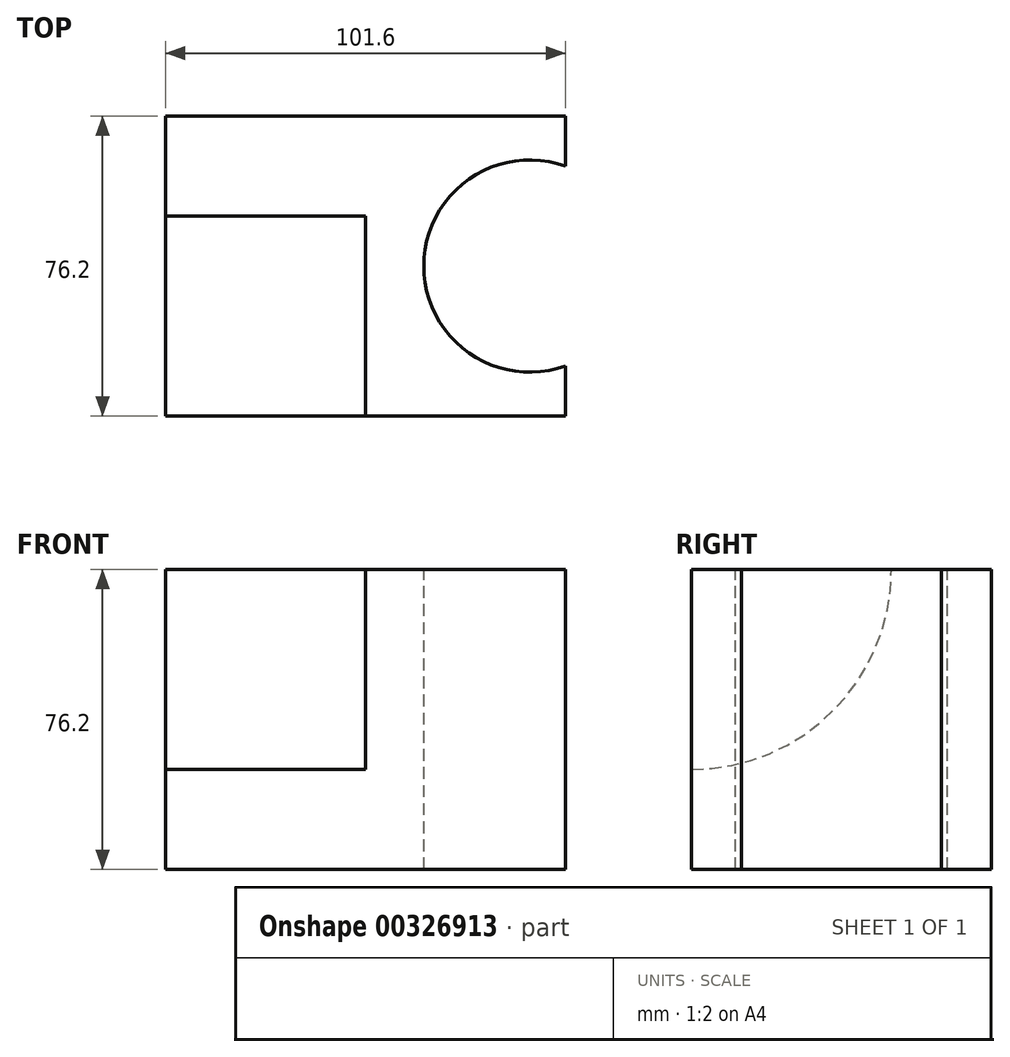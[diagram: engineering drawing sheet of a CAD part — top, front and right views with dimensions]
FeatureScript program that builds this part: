
annotation { "Feature Type Name" : "Feature", "Feature Type Description" : "" }
export const myFeature = defineFeature(function(context is Context, id is Id, definition is map)
    precondition{}
    {
        {
            var Q0;
            Q0=qCreatedBy(makeId("Front.planeOp"),FACE);
            var sketch = newSketch(context, id + "F0", { "sketchPlane" : qUnion([Q0])});
            skLineSegment(sketch, "E0", {"start": v(-48.15, -47.94) * mm, "end": v(53.45, -47.94) * mm});
            skLineSegment(sketch, "E1", {"start": v(-48.15, -47.94) * mm, "end": v(-48.15, -35.24) * mm});
            skLineSegment(sketch, "E2", {"start": v(-48.15, -35.24) * mm, "end": v(53.45, -35.24) * mm});
            skLineSegment(sketch, "E3", {"start": v(53.45, -35.24) * mm, "end": v(53.45, -47.94) * mm});
            skSolve(sketch);
        }
        {
            var Q0;
            Q0=makeQuery(id+"F0.imprint","IMPRINT",FACE,{"disambiguationData":[TD([[makeQuery(id+"F0.imprint","IMPRINT",EDGE,{"derivedFrom":sQuery(id+"F0.wireOp",EDGE,"E0")}),1.0]])]});
            extrude(context, id + "F1", {"entities" : qUnion([Q0]), "depth" : 76.2 * mm});
        }
        {
            var Q0;
            Q0=makeQuery(id+"F1.opExtrude","SWEPT_FACE",FACE,{"disambiguationData":[OSD([sQuery(id+"F0.wireOp",EDGE,"E2")])]});
            extrude(context, id + "F2", {"entities" : qUnion([Q0]), "operationType" : NewBodyOperationType.ADD, "depth" : 63.5 * mm});
        }
        {
            var Q0;
            Q0=makeQuery(id+"F2.opExtrude","CAP_FACE",FACE,{"disambiguationData":[OSD([sQuery(id+"F0.wireOp",EDGE,"E2")])],"isStart":false});
            var sketch = newSketch(context, id + "F3", { "sketchPlane" : qUnion([Q0])});
            skLineSegment(sketch, "E4", {"start": v(53.45, 0) * mm, "end": v(53.45, -12.7) * mm});
            skLineSegment(sketch, "E5", {"start": v(53.45, -76.2) * mm, "end": v(53.45, -63.5) * mm});
            skArc(sketch, "E6", {"start": v(53.45, -12.7) * mm, "mid": v(17.45, -38.1) * mm, "end": v(53.45, -63.5) * mm});
            skSolve(sketch);
        }
        {
            var Q0;
            {var subQ0=sQuery(id+"F3.wireOp",EDGE,"E6");Q0=makeQuery(id+"F3.imprint","IMPRINT",FACE,{"disambiguationData":[TD([[makeQuery(id+"F3.imprint","IMPRINT",EDGE,{"derivedFrom":subQ0}),1.0]])]});}
            extrude(context, id + "F4", {"entities" : qUnion([Q0]), "operationType" : NewBodyOperationType.REMOVE, "oppositeDirection" : true, "depth" : 127 * mm});
        }
        {
            var Q0;
            Q0=makeQuery(id+"F2.opExtrude","CAP_FACE",FACE,{"disambiguationData":[OSD([sQuery(id+"F0.wireOp",EDGE,"E2")])],"isStart":false});
            var sketch = newSketch(context, id + "F5", { "sketchPlane" : qUnion([Q0])});
            skLineSegment(sketch, "E7", {"start": v(-48.15, 0) * mm, "end": v(-48.15, -25.4) * mm});
            skLineSegment(sketch, "E8", {"start": v(-48.15, -25.4) * mm, "end": v(2.65, -25.4) * mm});
            skLineSegment(sketch, "E9", {"start": v(2.65, -25.4) * mm, "end": v(2.65, -76.2) * mm});
            skSolve(sketch);
        }
        {
            var Q0;
            {var subQ0=sQuery(id+"F5.wireOp",EDGE,"E8");Q0=makeQuery(id+"F5.imprint","IMPRINT",FACE,{"disambiguationData":[TD([[makeQuery(id+"F5.imprint","IMPRINT",EDGE,{"derivedFrom":subQ0}),-1.0]])]});}
            var Q1;
            {var subQ0=sQuery(id+"F0.wireOp",EDGE,"E2");Q1=makeQuery(id+"F2.opExtrude","CAP_EDGE",EDGE,{"disambiguationData":[OSD([subQ0]),TDD([makeQuery(id+"F1.opExtrude","CAP_EDGE",EDGE,{"disambiguationData":[OSD([subQ0])],"isStart":false})])],"isStart":false});}
            revolve(context, id + "F6", {"operationType" : NewBodyOperationType.REMOVE, "entities" : qUnion([Q0]), "axis" : qUnion([Q1]), "revolveType" : RevolveType.FULL, "oppositeDirection" : true});
        }
    });
